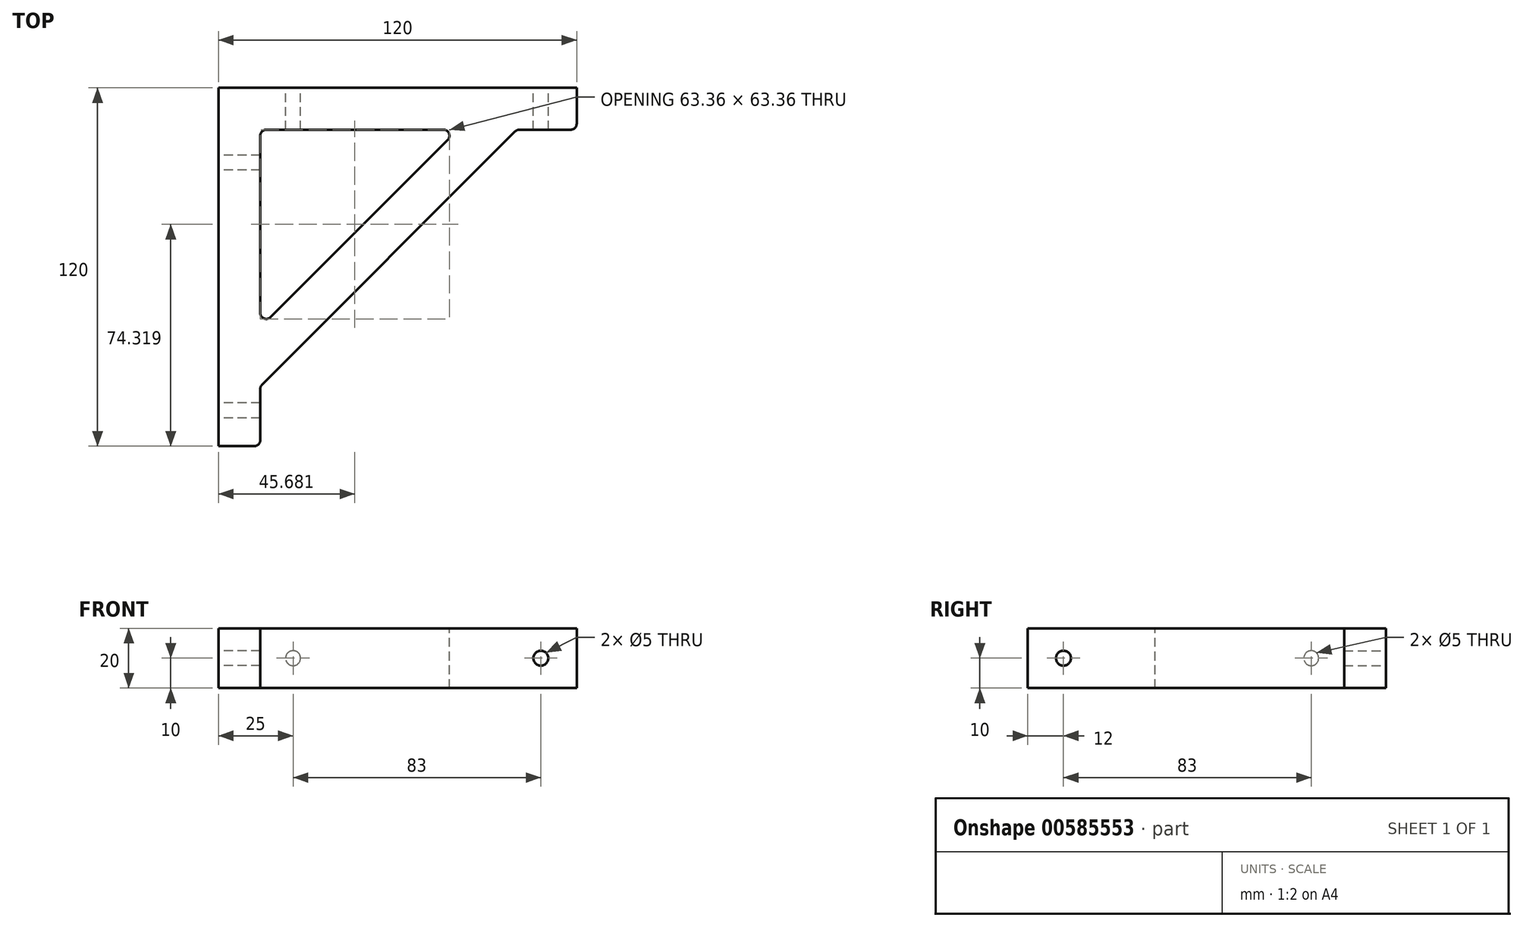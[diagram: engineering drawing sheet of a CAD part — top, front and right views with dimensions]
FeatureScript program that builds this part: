
annotation { "Feature Type Name" : "Feature", "Feature Type Description" : "" }
export const myFeature = defineFeature(function(context is Context, id is Id, definition is map)
    precondition{}
    {
        {
            var Q0;
            Q0=qCreatedBy(makeId("Top.planeOp"),FACE);
            var sketch = newSketch(context, id + "F0", { "sketchPlane" : qUnion([Q0])});
            skLineSegment(sketch, "E0", {"start": v(0, 0) * mm, "end": v(0, 120) * mm});
            skLineSegment(sketch, "E1", {"start": v(0, 120) * mm, "end": v(120, 120) * mm});
            skLineSegment(sketch, "E2", {"start": v(120, 120) * mm, "end": v(120, 106) * mm});
            skLineSegment(sketch, "E3", {"start": v(120, 106) * mm, "end": v(100, 106) * mm});
            skLineSegment(sketch, "E4", {"start": v(100, 106) * mm, "end": v(14, 20) * mm});
            skLineSegment(sketch, "E5", {"start": v(14, 20) * mm, "end": v(14, 0) * mm});
            skLineSegment(sketch, "E6", {"start": v(14, 0) * mm, "end": v(0, 0) * mm});
            skLineSegment(sketch, "E7", {"start": v(14, 106) * mm, "end": v(14, 39.8) * mm});
            skLineSegment(sketch, "E8", {"start": v(14, 39.8) * mm, "end": v(80.2, 106) * mm});
            skLineSegment(sketch, "E9", {"start": v(80.2, 106) * mm, "end": v(14, 106) * mm});
            skSolve(sketch);
        }
        {
            var Q0;
            Q0 = qSketchRegion(id + "F0", true);
            extrude(context, id + "F1", {"entities" : qUnion([Q0]), "depth" : 20 * mm, "offsetDistance" : 25 * mm});
        }
        {
            var Q0;
            Q0=makeQuery(id+"F1.opExtrude","SWEPT_FACE",FACE,{"disambiguationData":[OSD([sQuery(id+"F0.wireOp",EDGE,"E0")])]});
            var sketch = newSketch(context, id + "F2", { "sketchPlane" : qUnion([Q0])});
            skCircle(sketch, "E10", {"center": v(-12, 10) * mm, "radius": 2.5 * mm});
            skPoint(sketch, "E10.centerSnap0", {"position": v(0, 10) * mm});
            skCircle(sketch, "E11", {"center": v(-95, 10) * mm, "radius": 2.5 * mm});
            skSolve(sketch);
        }
        {
            var Q0;
            Q0 = qSketchRegion(id + "F2", true);
            extrude(context, id + "F3", {"entities" : qUnion([Q0]), "operationType" : NewBodyOperationType.REMOVE, "oppositeDirection" : true, "depth" : 25 * mm, "offsetDistance" : 25 * mm});
        }
        {
            var Q0;
            Q0=makeQuery(id+"F1.opExtrude","SWEPT_FACE",FACE,{"disambiguationData":[OSD([sQuery(id+"F0.wireOp",EDGE,"E1")])]});
            var sketch = newSketch(context, id + "F4", { "sketchPlane" : qUnion([Q0])});
            skCircle(sketch, "E12", {"center": v(-108, 10) * mm, "radius": 2.5 * mm});
            skPoint(sketch, "E12.centerSnap0", {"position": v(-120, 10) * mm});
            skCircle(sketch, "E13", {"center": v(-25, 10) * mm, "radius": 2.5 * mm});
            skSolve(sketch);
        }
        {
            var Q0;
            Q0 = qSketchRegion(id + "F4", true);
            extrude(context, id + "F5", {"entities" : qUnion([Q0]), "operationType" : NewBodyOperationType.REMOVE, "oppositeDirection" : true, "depth" : 25 * mm, "offsetDistance" : 25 * mm});
        }
        {
            var Q0;
            Q0=makeQuery(id+"F1.opExtrude","SWEPT_EDGE",EDGE,{"disambiguationData":[OSD([sQuery(id+"F0.wireOp",EDGE,"E7"),sQuery(id+"F0.wireOp",EDGE,"E8")])]});
            var Q1;
            Q1=makeQuery(id+"F1.opExtrude","SWEPT_EDGE",EDGE,{"disambiguationData":[OSD([sQuery(id+"F0.wireOp",EDGE,"E7"),sQuery(id+"F0.wireOp",EDGE,"E9")])]});
            var Q2;
            Q2=makeQuery(id+"F1.opExtrude","SWEPT_EDGE",EDGE,{"disambiguationData":[OSD([sQuery(id+"F0.wireOp",EDGE,"E8"),sQuery(id+"F0.wireOp",EDGE,"E9")])]});
            var Q3;
            Q3=makeQuery(id+"F1.opExtrude","SWEPT_EDGE",EDGE,{"disambiguationData":[OSD([sQuery(id+"F0.wireOp",EDGE,"E4"),sQuery(id+"F0.wireOp",EDGE,"E5")])]});
            var Q4;
            Q4=makeQuery(id+"F1.opExtrude","SWEPT_EDGE",EDGE,{"disambiguationData":[OSD([sQuery(id+"F0.wireOp",EDGE,"E3"),sQuery(id+"F0.wireOp",EDGE,"E4")])]});
            var Q5;
            Q5=makeQuery(id+"F1.opExtrude","SWEPT_EDGE",EDGE,{"disambiguationData":[OSD([sQuery(id+"F0.wireOp",EDGE,"E2"),sQuery(id+"F0.wireOp",EDGE,"E3")])]});
            var Q6;
            Q6=makeQuery(id+"F1.opExtrude","SWEPT_EDGE",EDGE,{"disambiguationData":[OSD([sQuery(id+"F0.wireOp",EDGE,"E5"),sQuery(id+"F0.wireOp",EDGE,"E6")])]});
            fillet(context, id + "F6", {"entities" : qUnion([Q0, Q1, Q2, Q3, Q4, Q5, Q6]), "radius" : 2 * mm, "tangentPropagation" : true, "allowEdgeOverflow" : false});
        }
    });
